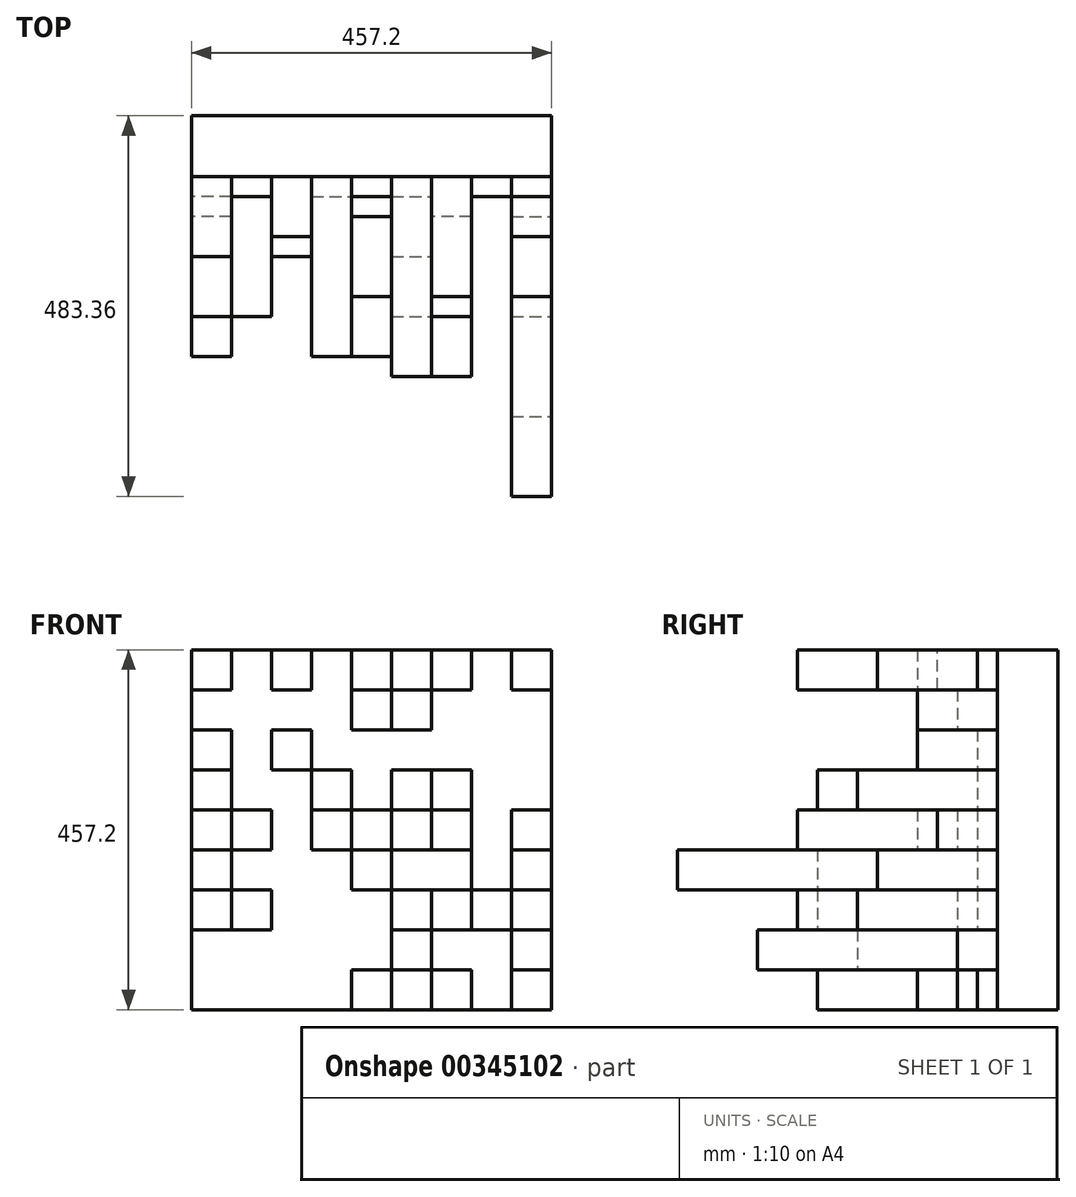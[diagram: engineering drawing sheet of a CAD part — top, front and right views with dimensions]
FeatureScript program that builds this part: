
annotation { "Feature Type Name" : "Feature", "Feature Type Description" : "" }
export const myFeature = defineFeature(function(context is Context, id is Id, definition is map)
    precondition{}
    {
        {
            var Q0;
            Q0=qCreatedBy(makeId("Front.planeOp"),FACE);
            var sketch = newSketch(context, id + "F0", { "sketchPlane" : qUnion([Q0])});
            skLineSegment(sketch, "E0.bottom", {"start": v(-369.5, 379.45) * mm, "end": v(87.7, 379.45) * mm});
            skLineSegment(sketch, "E0.top", {"start": v(-369.5, -77.75) * mm, "end": v(87.7, -77.75) * mm});
            skLineSegment(sketch, "E0.left", {"start": v(-369.5, 379.45) * mm, "end": v(-369.5, -77.75) * mm});
            skLineSegment(sketch, "E0.right", {"start": v(87.7, 379.45) * mm, "end": v(87.7, -77.75) * mm});
            skSolve(sketch);
        }
        {
            var Q0;
            Q0=makeQuery(id+"F0.imprint","IMPRINT",FACE,{"disambiguationData":[TD([[makeQuery(id+"F0.imprint","IMPRINT",EDGE,{"derivedFrom":sQuery(id+"F0.wireOp",EDGE,"E0.bottom")}),-1.0]])]});
            extrude(context, id + "F1", {"entities" : qUnion([Q0]), "depth" : 76.96 * mm});
        }
        {
            var Q0;
            Q0=makeQuery(id+"F1.opExtrude","CAP_FACE",FACE,{"disambiguationData":[OSD([sQuery(id+"F0.wireOp",EDGE,"E0.bottom"),sQuery(id+"F0.wireOp",EDGE,"E0.top"),sQuery(id+"F0.wireOp",EDGE,"E0.left"),sQuery(id+"F0.wireOp",EDGE,"E0.right")])],"isStart":false});
            var sketch = newSketch(context, id + "F2", { "sketchPlane" : qUnion([Q0])});
            skLineSegment(sketch, "E1.bottom", {"start": v(-369.5, 379.45) * mm, "end": v(-318.7, 379.45) * mm});
            skLineSegment(sketch, "E1.top", {"start": v(-369.5, 328.65) * mm, "end": v(-318.7, 328.65) * mm});
            skLineSegment(sketch, "E1.left", {"start": v(-369.5, 379.45) * mm, "end": v(-369.5, 328.65) * mm});
            skLineSegment(sketch, "E1.right", {"start": v(-318.7, 379.45) * mm, "end": v(-318.7, 328.65) * mm});
            skLineSegment(sketch, "E2.bottom", {"start": v(-318.7, 328.65) * mm, "end": v(-369.5, 328.65) * mm});
            skLineSegment(sketch, "E2.top", {"start": v(-318.7, 277.85) * mm, "end": v(-369.5, 277.85) * mm});
            skLineSegment(sketch, "E2.left", {"start": v(-318.7, 328.65) * mm, "end": v(-318.7, 277.85) * mm});
            skLineSegment(sketch, "E2.right", {"start": v(-369.5, 328.65) * mm, "end": v(-369.5, 277.85) * mm});
            skLineSegment(sketch, "E3.top", {"start": v(-318.7, 227.05) * mm, "end": v(-369.5, 227.05) * mm});
            skLineSegment(sketch, "E3.left", {"start": v(-318.7, 277.85) * mm, "end": v(-318.7, 227.05) * mm});
            skLineSegment(sketch, "E3.right", {"start": v(-369.5, 277.85) * mm, "end": v(-369.5, 227.05) * mm});
            skLineSegment(sketch, "E4.top", {"start": v(-318.7, 176.25) * mm, "end": v(-369.5, 176.25) * mm});
            skLineSegment(sketch, "E4.left", {"start": v(-318.7, 227.05) * mm, "end": v(-318.7, 176.25) * mm});
            skLineSegment(sketch, "E4.right", {"start": v(-369.5, 227.05) * mm, "end": v(-369.5, 176.25) * mm});
            skLineSegment(sketch, "E5.top", {"start": v(-318.7, 125.45) * mm, "end": v(-369.5, 125.45) * mm});
            skLineSegment(sketch, "E5.left", {"start": v(-318.7, 176.25) * mm, "end": v(-318.7, 125.45) * mm});
            skLineSegment(sketch, "E5.right", {"start": v(-369.5, 176.25) * mm, "end": v(-369.5, 125.45) * mm});
            skLineSegment(sketch, "E6.top", {"start": v(-318.7, 74.65) * mm, "end": v(-369.5, 74.65) * mm});
            skLineSegment(sketch, "E6.left", {"start": v(-318.7, 125.45) * mm, "end": v(-318.7, 74.65) * mm});
            skLineSegment(sketch, "E6.right", {"start": v(-369.5, 125.45) * mm, "end": v(-369.5, 74.65) * mm});
            skLineSegment(sketch, "E7.top", {"start": v(-318.7, 23.85) * mm, "end": v(-369.5, 23.85) * mm});
            skLineSegment(sketch, "E7.left", {"start": v(-318.7, 74.65) * mm, "end": v(-318.7, 23.85) * mm});
            skLineSegment(sketch, "E7.right", {"start": v(-369.5, 74.65) * mm, "end": v(-369.5, 23.85) * mm});
            skLineSegment(sketch, "E8.top", {"start": v(-318.7, -26.95) * mm, "end": v(-369.5, -26.95) * mm});
            skLineSegment(sketch, "E8.left", {"start": v(-318.7, 23.85) * mm, "end": v(-318.7, -26.95) * mm});
            skLineSegment(sketch, "E8.right", {"start": v(-369.5, 23.85) * mm, "end": v(-369.5, -26.95) * mm});
            skLineSegment(sketch, "E9.top", {"start": v(-318.7, -77.75) * mm, "end": v(-369.5, -77.75) * mm});
            skLineSegment(sketch, "E9.left", {"start": v(-318.7, -26.95) * mm, "end": v(-318.7, -77.75) * mm});
            skLineSegment(sketch, "E9.right", {"start": v(-369.5, -26.95) * mm, "end": v(-369.5, -77.75) * mm});
            skLineSegment(sketch, "E10.bottom", {"start": v(-318.7, -26.95) * mm, "end": v(-267.9, -26.95) * mm});
            skLineSegment(sketch, "E10.top", {"start": v(-318.7, 23.85) * mm, "end": v(-267.9, 23.85) * mm});
            skLineSegment(sketch, "E10.left", {"start": v(-318.7, -26.95) * mm, "end": v(-318.7, 23.85) * mm});
            skLineSegment(sketch, "E10.right", {"start": v(-267.9, -26.95) * mm, "end": v(-267.9, 23.85) * mm});
            skLineSegment(sketch, "E11.bottom", {"start": v(-267.9, -26.95) * mm, "end": v(-318.7, -26.95) * mm});
            skLineSegment(sketch, "E11.top", {"start": v(-267.9, -77.75) * mm, "end": v(-318.7, -77.75) * mm});
            skLineSegment(sketch, "E11.left", {"start": v(-267.9, -26.95) * mm, "end": v(-267.9, -77.75) * mm});
            skLineSegment(sketch, "E12.top", {"start": v(-318.7, 74.65) * mm, "end": v(-267.9, 74.65) * mm});
            skLineSegment(sketch, "E12.left", {"start": v(-318.7, 23.85) * mm, "end": v(-318.7, 74.65) * mm});
            skLineSegment(sketch, "E12.right", {"start": v(-267.9, 23.85) * mm, "end": v(-267.9, 74.65) * mm});
            skLineSegment(sketch, "E13.top", {"start": v(-318.7, 125.45) * mm, "end": v(-267.9, 125.45) * mm});
            skLineSegment(sketch, "E13.left", {"start": v(-318.7, 74.65) * mm, "end": v(-318.7, 125.45) * mm});
            skLineSegment(sketch, "E13.right", {"start": v(-267.9, 74.65) * mm, "end": v(-267.9, 125.45) * mm});
            skLineSegment(sketch, "E14.top", {"start": v(-318.7, 176.25) * mm, "end": v(-267.9, 176.25) * mm});
            skLineSegment(sketch, "E14.left", {"start": v(-318.7, 125.45) * mm, "end": v(-318.7, 176.25) * mm});
            skLineSegment(sketch, "E14.right", {"start": v(-267.9, 125.45) * mm, "end": v(-267.9, 176.25) * mm});
            skLineSegment(sketch, "E15.top", {"start": v(-318.7, 227.05) * mm, "end": v(-267.9, 227.05) * mm});
            skLineSegment(sketch, "E15.left", {"start": v(-318.7, 176.25) * mm, "end": v(-318.7, 227.05) * mm});
            skLineSegment(sketch, "E15.right", {"start": v(-267.9, 176.25) * mm, "end": v(-267.9, 227.05) * mm});
            skLineSegment(sketch, "E16.top", {"start": v(-318.7, 277.85) * mm, "end": v(-267.9, 277.85) * mm});
            skLineSegment(sketch, "E16.left", {"start": v(-318.7, 227.05) * mm, "end": v(-318.7, 277.85) * mm});
            skLineSegment(sketch, "E16.right", {"start": v(-267.9, 227.05) * mm, "end": v(-267.9, 277.85) * mm});
            skLineSegment(sketch, "E17.top", {"start": v(-318.7, 328.65) * mm, "end": v(-267.9, 328.65) * mm});
            skLineSegment(sketch, "E17.left", {"start": v(-318.7, 277.85) * mm, "end": v(-318.7, 328.65) * mm});
            skLineSegment(sketch, "E17.right", {"start": v(-267.9, 277.85) * mm, "end": v(-267.9, 328.65) * mm});
            skLineSegment(sketch, "E18.top", {"start": v(-318.7, 379.45) * mm, "end": v(-267.9, 379.45) * mm});
            skLineSegment(sketch, "E18.left", {"start": v(-318.7, 328.65) * mm, "end": v(-318.7, 379.45) * mm});
            skLineSegment(sketch, "E18.right", {"start": v(-267.9, 328.65) * mm, "end": v(-267.9, 379.45) * mm});
            skLineSegment(sketch, "E19.bottom", {"start": v(-267.9, 227.05) * mm, "end": v(-217.1, 227.05) * mm});
            skLineSegment(sketch, "E19.top", {"start": v(-267.9, 176.25) * mm, "end": v(-217.1, 176.25) * mm});
            skLineSegment(sketch, "E19.left", {"start": v(-267.9, 227.05) * mm, "end": v(-267.9, 176.25) * mm});
            skLineSegment(sketch, "E19.right", {"start": v(-217.1, 227.05) * mm, "end": v(-217.1, 176.25) * mm});
            skLineSegment(sketch, "E20.top", {"start": v(-267.9, 277.85) * mm, "end": v(-217.1, 277.85) * mm});
            skLineSegment(sketch, "E20.right", {"start": v(-217.1, 227.05) * mm, "end": v(-217.1, 277.85) * mm});
            skLineSegment(sketch, "E21.top", {"start": v(-267.9, 328.65) * mm, "end": v(-217.1, 328.65) * mm});
            skLineSegment(sketch, "E21.right", {"start": v(-217.1, 277.85) * mm, "end": v(-217.1, 328.65) * mm});
            skLineSegment(sketch, "E22.top", {"start": v(-267.9, 379.45) * mm, "end": v(-217.1, 379.45) * mm});
            skLineSegment(sketch, "E22.right", {"start": v(-217.1, 328.65) * mm, "end": v(-217.1, 379.45) * mm});
            skLineSegment(sketch, "E23.top", {"start": v(-267.9, 125.45) * mm, "end": v(-217.1, 125.45) * mm});
            skLineSegment(sketch, "E23.left", {"start": v(-267.9, 176.25) * mm, "end": v(-267.9, 125.45) * mm});
            skLineSegment(sketch, "E23.right", {"start": v(-217.1, 176.25) * mm, "end": v(-217.1, 125.45) * mm});
            skLineSegment(sketch, "E24.top", {"start": v(-267.9, 74.65) * mm, "end": v(-217.1, 74.65) * mm});
            skLineSegment(sketch, "E24.left", {"start": v(-267.9, 125.45) * mm, "end": v(-267.9, 74.65) * mm});
            skLineSegment(sketch, "E24.right", {"start": v(-217.1, 125.45) * mm, "end": v(-217.1, 74.65) * mm});
            skLineSegment(sketch, "E25.top", {"start": v(-267.9, 23.85) * mm, "end": v(-217.1, 23.85) * mm});
            skLineSegment(sketch, "E25.left", {"start": v(-267.9, 74.65) * mm, "end": v(-267.9, 23.85) * mm});
            skLineSegment(sketch, "E25.right", {"start": v(-217.1, 74.65) * mm, "end": v(-217.1, 23.85) * mm});
            skLineSegment(sketch, "E26.top", {"start": v(-267.9, -26.95) * mm, "end": v(-217.1, -26.95) * mm});
            skLineSegment(sketch, "E26.left", {"start": v(-267.9, 23.85) * mm, "end": v(-267.9, -26.95) * mm});
            skLineSegment(sketch, "E26.right", {"start": v(-217.1, 23.85) * mm, "end": v(-217.1, -26.95) * mm});
            skLineSegment(sketch, "E27.top", {"start": v(-267.9, -77.75) * mm, "end": v(-217.1, -77.75) * mm});
            skLineSegment(sketch, "E27.right", {"start": v(-217.1, -26.95) * mm, "end": v(-217.1, -77.75) * mm});
            skLineSegment(sketch, "E28.bottom", {"start": v(-217.1, 328.65) * mm, "end": v(-166.3, 328.65) * mm});
            skLineSegment(sketch, "E28.top", {"start": v(-217.1, 379.45) * mm, "end": v(-166.3, 379.45) * mm});
            skLineSegment(sketch, "E28.right", {"start": v(-166.3, 328.65) * mm, "end": v(-166.3, 379.45) * mm});
            skLineSegment(sketch, "E29.top", {"start": v(-217.1, 277.85) * mm, "end": v(-166.3, 277.85) * mm});
            skLineSegment(sketch, "E29.left", {"start": v(-217.1, 328.65) * mm, "end": v(-217.1, 277.85) * mm});
            skLineSegment(sketch, "E29.right", {"start": v(-166.3, 328.65) * mm, "end": v(-166.3, 277.85) * mm});
            skLineSegment(sketch, "E30.top", {"start": v(-217.1, 227.05) * mm, "end": v(-166.3, 227.05) * mm});
            skLineSegment(sketch, "E30.left", {"start": v(-217.1, 277.85) * mm, "end": v(-217.1, 227.05) * mm});
            skLineSegment(sketch, "E30.right", {"start": v(-166.3, 277.85) * mm, "end": v(-166.3, 227.05) * mm});
            skLineSegment(sketch, "E31.top", {"start": v(-217.1, 176.25) * mm, "end": v(-166.3, 176.25) * mm});
            skLineSegment(sketch, "E31.right", {"start": v(-166.3, 227.05) * mm, "end": v(-166.3, 176.25) * mm});
            skLineSegment(sketch, "E32.top", {"start": v(-217.1, 125.45) * mm, "end": v(-166.3, 125.45) * mm});
            skLineSegment(sketch, "E32.right", {"start": v(-166.3, 176.25) * mm, "end": v(-166.3, 125.45) * mm});
            skLineSegment(sketch, "E33.top", {"start": v(-217.1, 74.65) * mm, "end": v(-166.3, 74.65) * mm});
            skLineSegment(sketch, "E33.right", {"start": v(-166.3, 125.45) * mm, "end": v(-166.3, 74.65) * mm});
            skLineSegment(sketch, "E34.top", {"start": v(-217.1, 23.85) * mm, "end": v(-166.3, 23.85) * mm});
            skLineSegment(sketch, "E34.right", {"start": v(-166.3, 74.65) * mm, "end": v(-166.3, 23.85) * mm});
            skLineSegment(sketch, "E35.top", {"start": v(-217.1, -26.95) * mm, "end": v(-166.3, -26.95) * mm});
            skLineSegment(sketch, "E35.right", {"start": v(-166.3, 23.85) * mm, "end": v(-166.3, -26.95) * mm});
            skLineSegment(sketch, "E36.top", {"start": v(-217.1, -77.75) * mm, "end": v(-166.3, -77.75) * mm});
            skLineSegment(sketch, "E36.right", {"start": v(-166.3, -26.95) * mm, "end": v(-166.3, -77.75) * mm});
            skLineSegment(sketch, "E37.bottom", {"start": v(-166.3, 328.65) * mm, "end": v(-115.5, 328.65) * mm});
            skLineSegment(sketch, "E37.top", {"start": v(-166.3, 379.45) * mm, "end": v(-115.5, 379.45) * mm});
            skLineSegment(sketch, "E37.right", {"start": v(-115.5, 328.65) * mm, "end": v(-115.5, 379.45) * mm});
            skLineSegment(sketch, "E38.top", {"start": v(-166.3, 277.85) * mm, "end": v(-115.5, 277.85) * mm});
            skLineSegment(sketch, "E38.right", {"start": v(-115.5, 328.65) * mm, "end": v(-115.5, 277.85) * mm});
            skLineSegment(sketch, "E39.top", {"start": v(-166.3, 227.05) * mm, "end": v(-115.5, 227.05) * mm});
            skLineSegment(sketch, "E39.right", {"start": v(-115.5, 277.85) * mm, "end": v(-115.5, 227.05) * mm});
            skLineSegment(sketch, "E40.top", {"start": v(-166.3, 176.25) * mm, "end": v(-115.5, 176.25) * mm});
            skLineSegment(sketch, "E40.right", {"start": v(-115.5, 227.05) * mm, "end": v(-115.5, 176.25) * mm});
            skLineSegment(sketch, "E41.top", {"start": v(-166.3, 125.45) * mm, "end": v(-115.5, 125.45) * mm});
            skLineSegment(sketch, "E41.right", {"start": v(-115.5, 176.25) * mm, "end": v(-115.5, 125.45) * mm});
            skLineSegment(sketch, "E42.top", {"start": v(-166.3, 74.65) * mm, "end": v(-115.5, 74.65) * mm});
            skLineSegment(sketch, "E42.right", {"start": v(-115.5, 125.45) * mm, "end": v(-115.5, 74.65) * mm});
            skLineSegment(sketch, "E43.top", {"start": v(-166.3, 23.85) * mm, "end": v(-115.5, 23.85) * mm});
            skLineSegment(sketch, "E43.right", {"start": v(-115.5, 74.65) * mm, "end": v(-115.5, 23.85) * mm});
            skLineSegment(sketch, "E44.top", {"start": v(-166.3, -26.95) * mm, "end": v(-115.5, -26.95) * mm});
            skLineSegment(sketch, "E44.right", {"start": v(-115.5, 23.85) * mm, "end": v(-115.5, -26.95) * mm});
            skLineSegment(sketch, "E45.top", {"start": v(-166.3, -77.75) * mm, "end": v(-115.5, -77.75) * mm});
            skLineSegment(sketch, "E45.right", {"start": v(-115.5, -26.95) * mm, "end": v(-115.5, -77.75) * mm});
            skLineSegment(sketch, "E46.bottom", {"start": v(-115.5, -26.95) * mm, "end": v(-64.7, -26.95) * mm});
            skLineSegment(sketch, "E46.top", {"start": v(-115.5, -77.75) * mm, "end": v(-64.7, -77.75) * mm});
            skLineSegment(sketch, "E46.right", {"start": v(-64.7, -26.95) * mm, "end": v(-64.7, -77.75) * mm});
            skLineSegment(sketch, "E47.bottom", {"start": v(-115.5, 23.85) * mm, "end": v(-64.7, 23.85) * mm});
            skLineSegment(sketch, "E47.right", {"start": v(-64.7, 23.85) * mm, "end": v(-64.7, -26.95) * mm});
            skLineSegment(sketch, "E48.bottom", {"start": v(-115.5, 74.65) * mm, "end": v(-64.7, 74.65) * mm});
            skLineSegment(sketch, "E48.right", {"start": v(-64.7, 74.65) * mm, "end": v(-64.7, 23.85) * mm});
            skLineSegment(sketch, "E49.bottom", {"start": v(-115.5, 125.45) * mm, "end": v(-64.7, 125.45) * mm});
            skLineSegment(sketch, "E49.right", {"start": v(-64.7, 125.45) * mm, "end": v(-64.7, 74.65) * mm});
            skLineSegment(sketch, "E50.bottom", {"start": v(-115.5, 176.25) * mm, "end": v(-64.7, 176.25) * mm});
            skLineSegment(sketch, "E50.right", {"start": v(-64.7, 176.25) * mm, "end": v(-64.7, 125.45) * mm});
            skLineSegment(sketch, "E51.bottom", {"start": v(-115.5, 227.05) * mm, "end": v(-64.7, 227.05) * mm});
            skLineSegment(sketch, "E51.right", {"start": v(-64.7, 227.05) * mm, "end": v(-64.7, 176.25) * mm});
            skLineSegment(sketch, "E52.bottom", {"start": v(-115.5, 277.85) * mm, "end": v(-64.7, 277.85) * mm});
            skLineSegment(sketch, "E52.right", {"start": v(-64.7, 277.85) * mm, "end": v(-64.7, 227.05) * mm});
            skLineSegment(sketch, "E53.bottom", {"start": v(-115.5, 328.65) * mm, "end": v(-64.7, 328.65) * mm});
            skLineSegment(sketch, "E53.right", {"start": v(-64.7, 328.65) * mm, "end": v(-64.7, 277.85) * mm});
            skLineSegment(sketch, "E54.bottom", {"start": v(-115.5, 379.45) * mm, "end": v(-64.7, 379.45) * mm});
            skLineSegment(sketch, "E54.left", {"start": v(-115.5, 379.45) * mm, "end": v(-115.5, 328.65) * mm});
            skLineSegment(sketch, "E54.right", {"start": v(-64.7, 379.45) * mm, "end": v(-64.7, 328.65) * mm});
            skLineSegment(sketch, "E55.bottom", {"start": v(87.7, 379.45) * mm, "end": v(36.9, 379.45) * mm});
            skLineSegment(sketch, "E55.top", {"start": v(87.7, 328.65) * mm, "end": v(36.9, 328.65) * mm});
            skLineSegment(sketch, "E55.left", {"start": v(87.7, 379.45) * mm, "end": v(87.7, 328.65) * mm});
            skLineSegment(sketch, "E55.right", {"start": v(36.9, 379.45) * mm, "end": v(36.9, 328.65) * mm});
            skLineSegment(sketch, "E56.bottom", {"start": v(36.9, 328.65) * mm, "end": v(-13.9, 328.65) * mm});
            skLineSegment(sketch, "E56.top", {"start": v(36.9, 379.45) * mm, "end": v(-13.9, 379.45) * mm});
            skLineSegment(sketch, "E56.left", {"start": v(36.9, 328.65) * mm, "end": v(36.9, 379.45) * mm});
            skLineSegment(sketch, "E56.right", {"start": v(-13.9, 328.65) * mm, "end": v(-13.9, 379.45) * mm});
            skLineSegment(sketch, "E57.bottom", {"start": v(-13.9, 328.65) * mm, "end": v(-64.7, 328.65) * mm});
            skLineSegment(sketch, "E57.top", {"start": v(-13.9, 379.45) * mm, "end": v(-64.7, 379.45) * mm});
            skLineSegment(sketch, "E57.right", {"start": v(-64.7, 328.65) * mm, "end": v(-64.7, 379.45) * mm});
            skLineSegment(sketch, "E58.bottom", {"start": v(-64.7, 328.65) * mm, "end": v(-13.9, 328.65) * mm});
            skLineSegment(sketch, "E58.top", {"start": v(-64.7, 277.85) * mm, "end": v(-13.9, 277.85) * mm});
            skLineSegment(sketch, "E58.right", {"start": v(-13.9, 328.65) * mm, "end": v(-13.9, 277.85) * mm});
            skLineSegment(sketch, "E59.bottom", {"start": v(-13.9, 328.65) * mm, "end": v(36.9, 328.65) * mm});
            skLineSegment(sketch, "E59.top", {"start": v(-13.9, 277.85) * mm, "end": v(36.9, 277.85) * mm});
            skLineSegment(sketch, "E59.right", {"start": v(36.9, 328.65) * mm, "end": v(36.9, 277.85) * mm});
            skLineSegment(sketch, "E60.bottom", {"start": v(36.9, 328.65) * mm, "end": v(87.7, 328.65) * mm});
            skLineSegment(sketch, "E60.top", {"start": v(36.9, 277.85) * mm, "end": v(87.7, 277.85) * mm});
            skLineSegment(sketch, "E60.right", {"start": v(87.7, 328.65) * mm, "end": v(87.7, 277.85) * mm});
            skLineSegment(sketch, "E61.bottom", {"start": v(-13.9, 277.85) * mm, "end": v(-64.7, 277.85) * mm});
            skLineSegment(sketch, "E61.top", {"start": v(-13.9, 227.05) * mm, "end": v(-64.7, 227.05) * mm});
            skLineSegment(sketch, "E61.left", {"start": v(-13.9, 277.85) * mm, "end": v(-13.9, 227.05) * mm});
            skLineSegment(sketch, "E62.top", {"start": v(-13.9, 176.25) * mm, "end": v(-64.7, 176.25) * mm});
            skLineSegment(sketch, "E62.left", {"start": v(-13.9, 227.05) * mm, "end": v(-13.9, 176.25) * mm});
            skLineSegment(sketch, "E63.top", {"start": v(-13.9, 125.45) * mm, "end": v(-64.7, 125.45) * mm});
            skLineSegment(sketch, "E63.left", {"start": v(-13.9, 176.25) * mm, "end": v(-13.9, 125.45) * mm});
            skLineSegment(sketch, "E64.top", {"start": v(-13.9, 74.65) * mm, "end": v(-64.7, 74.65) * mm});
            skLineSegment(sketch, "E64.left", {"start": v(-13.9, 125.45) * mm, "end": v(-13.9, 74.65) * mm});
            skLineSegment(sketch, "E65.top", {"start": v(-13.9, 23.85) * mm, "end": v(-64.7, 23.85) * mm});
            skLineSegment(sketch, "E65.left", {"start": v(-13.9, 74.65) * mm, "end": v(-13.9, 23.85) * mm});
            skLineSegment(sketch, "E66.top", {"start": v(-13.9, -26.95) * mm, "end": v(-64.7, -26.95) * mm});
            skLineSegment(sketch, "E66.left", {"start": v(-13.9, 23.85) * mm, "end": v(-13.9, -26.95) * mm});
            skLineSegment(sketch, "E67.top", {"start": v(-13.9, 227.05) * mm, "end": v(36.9, 227.05) * mm});
            skLineSegment(sketch, "E67.right", {"start": v(36.9, 277.85) * mm, "end": v(36.9, 227.05) * mm});
            skLineSegment(sketch, "E68.top", {"start": v(36.9, 227.05) * mm, "end": v(87.7, 227.05) * mm});
            skLineSegment(sketch, "E68.right", {"start": v(87.7, 277.85) * mm, "end": v(87.7, 227.05) * mm});
            skLineSegment(sketch, "E69.bottom", {"start": v(36.9, 227.05) * mm, "end": v(-13.9, 227.05) * mm});
            skLineSegment(sketch, "E69.top", {"start": v(36.9, 176.25) * mm, "end": v(-13.9, 176.25) * mm});
            skLineSegment(sketch, "E69.left", {"start": v(36.9, 227.05) * mm, "end": v(36.9, 176.25) * mm});
            skLineSegment(sketch, "E70.bottom", {"start": v(-13.9, 176.25) * mm, "end": v(36.9, 176.25) * mm});
            skLineSegment(sketch, "E70.top", {"start": v(-13.9, 125.45) * mm, "end": v(36.9, 125.45) * mm});
            skLineSegment(sketch, "E70.right", {"start": v(36.9, 176.25) * mm, "end": v(36.9, 125.45) * mm});
            skLineSegment(sketch, "E71.bottom", {"start": v(-13.9, 74.65) * mm, "end": v(36.9, 74.65) * mm});
            skLineSegment(sketch, "E71.left", {"start": v(-13.9, 74.65) * mm, "end": v(-13.9, 125.45) * mm});
            skLineSegment(sketch, "E71.right", {"start": v(36.9, 74.65) * mm, "end": v(36.9, 125.45) * mm});
            skLineSegment(sketch, "E72.bottom", {"start": v(-13.9, 23.85) * mm, "end": v(36.9, 23.85) * mm});
            skLineSegment(sketch, "E72.left", {"start": v(-13.9, 23.85) * mm, "end": v(-13.9, 74.65) * mm});
            skLineSegment(sketch, "E72.right", {"start": v(36.9, 23.85) * mm, "end": v(36.9, 74.65) * mm});
            skLineSegment(sketch, "E73.top", {"start": v(-13.9, -77.75) * mm, "end": v(-64.7, -77.75) * mm});
            skLineSegment(sketch, "E73.left", {"start": v(-13.9, -26.95) * mm, "end": v(-13.9, -77.75) * mm});
            skLineSegment(sketch, "E74.bottom", {"start": v(-13.9, -26.95) * mm, "end": v(36.9, -26.95) * mm});
            skLineSegment(sketch, "E74.left", {"start": v(-13.9, -26.95) * mm, "end": v(-13.9, 23.85) * mm});
            skLineSegment(sketch, "E74.right", {"start": v(36.9, -26.95) * mm, "end": v(36.9, 23.85) * mm});
            skLineSegment(sketch, "E75.top", {"start": v(-13.9, -77.75) * mm, "end": v(36.9, -77.75) * mm});
            skLineSegment(sketch, "E75.right", {"start": v(36.9, -26.95) * mm, "end": v(36.9, -77.75) * mm});
            skLineSegment(sketch, "E76.bottom", {"start": v(36.9, -26.95) * mm, "end": v(87.7, -26.95) * mm});
            skLineSegment(sketch, "E76.top", {"start": v(36.9, -77.75) * mm, "end": v(87.7, -77.75) * mm});
            skLineSegment(sketch, "E76.right", {"start": v(87.7, -26.95) * mm, "end": v(87.7, -77.75) * mm});
            skLineSegment(sketch, "E77.top", {"start": v(36.9, 23.85) * mm, "end": v(87.7, 23.85) * mm});
            skLineSegment(sketch, "E77.right", {"start": v(87.7, -26.95) * mm, "end": v(87.7, 23.85) * mm});
            skLineSegment(sketch, "E78.top", {"start": v(36.9, 74.65) * mm, "end": v(87.7, 74.65) * mm});
            skLineSegment(sketch, "E78.right", {"start": v(87.7, 23.85) * mm, "end": v(87.7, 74.65) * mm});
            skLineSegment(sketch, "E79.top", {"start": v(36.9, 125.45) * mm, "end": v(87.7, 125.45) * mm});
            skLineSegment(sketch, "E79.right", {"start": v(87.7, 74.65) * mm, "end": v(87.7, 125.45) * mm});
            skLineSegment(sketch, "E80.top", {"start": v(36.9, 176.25) * mm, "end": v(87.7, 176.25) * mm});
            skLineSegment(sketch, "E80.left", {"start": v(36.9, 125.45) * mm, "end": v(36.9, 176.25) * mm});
            skLineSegment(sketch, "E80.right", {"start": v(87.7, 125.45) * mm, "end": v(87.7, 176.25) * mm});
            skLineSegment(sketch, "E81.left", {"start": v(36.9, 176.25) * mm, "end": v(36.9, 227.05) * mm});
            skLineSegment(sketch, "E81.right", {"start": v(87.7, 176.25) * mm, "end": v(87.7, 227.05) * mm});
            skSolve(sketch);
        }
        {
            var Q0;
            Q0=makeQuery(id+"F2.imprint","IMPRINT",FACE,{"disambiguationData":[TD([[makeQuery(id+"F2.imprint","IMPRINT",EDGE,{"derivedFrom":sQuery(id+"F2.wireOp",EDGE,"E1.bottom")}),-1.0]])]});
            var Q1;
            Q1=makeQuery(id+"F2.imprint","IMPRINT",FACE,{"disambiguationData":[TD([[makeQuery(id+"F2.imprint","IMPRINT",EDGE,{"derivedFrom":sQuery(id+"F2.wireOp",EDGE,"E19.bottom")}),1.0]])]});
            var Q2;
            Q2=makeQuery(id+"F2.imprint","IMPRINT",FACE,{"disambiguationData":[TD([[makeQuery(id+"F2.imprint","IMPRINT",EDGE,{"derivedFrom":sQuery(id+"F2.wireOp",EDGE,"E49.bottom")}),1.0]])]});
            var Q3;
            Q3=makeQuery(id+"F2.imprint","IMPRINT",FACE,{"disambiguationData":[TD([[makeQuery(id+"F2.imprint","IMPRINT",EDGE,{"derivedFrom":sQuery(id+"F2.wireOp",EDGE,"E33.top")}),-1.0]])]});
            var Q4;
            Q4=makeQuery(id+"F2.imprint","IMPRINT",FACE,{"disambiguationData":[TD([[makeQuery(id+"F2.imprint","IMPRINT",EDGE,{"derivedFrom":sQuery(id+"F2.wireOp",EDGE,"E7.top")}),1.0]])]});
            var Q5;
            Q5=makeQuery(id+"F2.imprint","IMPRINT",FACE,{"disambiguationData":[TD([[makeQuery(id+"F2.imprint","IMPRINT",EDGE,{"derivedFrom":sQuery(id+"F2.wireOp",EDGE,"E46.top")}),1.0]])]});
            var Q6;
            Q6=makeQuery(id+"F2.imprint","IMPRINT",FACE,{"disambiguationData":[TD([[makeQuery(id+"F2.imprint","IMPRINT",EDGE,{"derivedFrom":sQuery(id+"F2.wireOp",EDGE,"E80.top")}),1.0]])]});
            var Q7;
            Q7=makeQuery(id+"F2.imprint","IMPRINT",FACE,{"disambiguationData":[TD([[makeQuery(id+"F2.imprint","IMPRINT",EDGE,{"derivedFrom":sQuery(id+"F2.wireOp",EDGE,"E52.bottom")}),1.0]])]});
            extrude(context, id + "F3", {"entities" : qUnion([Q0, Q1, Q2, Q3, Q4, Q5, Q6, Q7]), "depth" : 101.6 * mm});
        }
        {
            var Q0;
            Q0=makeQuery(id+"F2.imprint","IMPRINT",FACE,{"disambiguationData":[TD([[makeQuery(id+"F2.imprint","IMPRINT",EDGE,{"derivedFrom":sQuery(id+"F2.wireOp",EDGE,"E2.top")}),1.0]])]});
            var Q1;
            Q1=makeQuery(id+"F2.imprint","IMPRINT",FACE,{"disambiguationData":[TD([[makeQuery(id+"F2.imprint","IMPRINT",EDGE,{"derivedFrom":sQuery(id+"F2.wireOp",EDGE,"E31.top")}),-1.0]])]});
            var Q2;
            Q2=makeQuery(id+"F2.imprint","IMPRINT",FACE,{"disambiguationData":[TD([[makeQuery(id+"F2.imprint","IMPRINT",EDGE,{"derivedFrom":sQuery(id+"F2.wireOp",EDGE,"E50.bottom")}),1.0]])]});
            var Q3;
            Q3=makeQuery(id+"F2.imprint","IMPRINT",FACE,{"disambiguationData":[TD([[makeQuery(id+"F2.imprint","IMPRINT",EDGE,{"derivedFrom":sQuery(id+"F2.wireOp",EDGE,"E55.bottom")}),-1.0]])]});
            var Q4;
            Q4=makeQuery(id+"F2.imprint","IMPRINT",FACE,{"disambiguationData":[TD([[makeQuery(id+"F2.imprint","IMPRINT",EDGE,{"derivedFrom":sQuery(id+"F2.wireOp",EDGE,"E37.top")}),-1.0]])]});
            var Q5;
            Q5=makeQuery(id+"F2.imprint","IMPRINT",FACE,{"disambiguationData":[TD([[makeQuery(id+"F2.imprint","IMPRINT",EDGE,{"derivedFrom":sQuery(id+"F2.wireOp",EDGE,"E35.top")}),-1.0]])]});
            var Q6;
            Q6=makeQuery(id+"F2.imprint","IMPRINT",FACE,{"disambiguationData":[TD([[makeQuery(id+"F2.imprint","IMPRINT",EDGE,{"derivedFrom":sQuery(id+"F2.wireOp",EDGE,"E71.bottom")}),-1.0]])]});
            var Q7;
            Q7=makeQuery(id+"F2.imprint","IMPRINT",FACE,{"disambiguationData":[TD([[makeQuery(id+"F2.imprint","IMPRINT",EDGE,{"derivedFrom":sQuery(id+"F2.wireOp",EDGE,"E76.top")}),1.0]])]});
            var Q8;
            Q8=makeQuery(id+"F2.imprint","IMPRINT",FACE,{"disambiguationData":[TD([[makeQuery(id+"F2.imprint","IMPRINT",EDGE,{"derivedFrom":sQuery(id+"F2.wireOp",EDGE,"E13.top")}),1.0]])]});
            var Q9;
            Q9=makeQuery(id+"F2.imprint","IMPRINT",FACE,{"disambiguationData":[TD([[makeQuery(id+"F2.imprint","IMPRINT",EDGE,{"derivedFrom":sQuery(id+"F2.wireOp",EDGE,"E5.top")}),1.0]])]});
            extrude(context, id + "F4", {"entities" : qUnion([Q0, Q1, Q2, Q3, Q4, Q5, Q6, Q7, Q8, Q9]), "depth" : 25.4 * mm});
        }
        {
            var Q0;
            Q0=makeQuery(id+"F2.imprint","IMPRINT",FACE,{"disambiguationData":[TD([[makeQuery(id+"F2.imprint","IMPRINT",EDGE,{"derivedFrom":sQuery(id+"F2.wireOp",EDGE,"E28.bottom")}),-1.0]])]});
            var Q1;
            Q1=makeQuery(id+"F2.imprint","IMPRINT",FACE,{"disambiguationData":[TD([[makeQuery(id+"F2.imprint","IMPRINT",EDGE,{"derivedFrom":sQuery(id+"F2.wireOp",EDGE,"E60.top")}),-1.0]])]});
            var Q2;
            Q2=makeQuery(id+"F2.imprint","IMPRINT",FACE,{"disambiguationData":[TD([[makeQuery(id+"F2.imprint","IMPRINT",EDGE,{"derivedFrom":sQuery(id+"F2.wireOp",EDGE,"E57.top")}),-1.0]])]});
            var Q3;
            Q3=makeQuery(id+"F2.imprint","IMPRINT",FACE,{"disambiguationData":[TD([[makeQuery(id+"F2.imprint","IMPRINT",EDGE,{"derivedFrom":sQuery(id+"F2.wireOp",EDGE,"E11.bottom")}),1.0]])]});
            var Q4;
            Q4=makeQuery(id+"F2.imprint","IMPRINT",FACE,{"disambiguationData":[TD([[makeQuery(id+"F2.imprint","IMPRINT",EDGE,{"derivedFrom":sQuery(id+"F2.wireOp",EDGE,"E41.top")}),-1.0]])]});
            var Q5;
            Q5=makeQuery(id+"F2.imprint","IMPRINT",FACE,{"disambiguationData":[TD([[makeQuery(id+"F2.imprint","IMPRINT",EDGE,{"derivedFrom":sQuery(id+"F2.wireOp",EDGE,"E78.top")}),1.0]])]});
            extrude(context, id + "F5", {"entities" : qUnion([Q0, Q1, Q2, Q3, Q4, Q5]), "depth" : 152.4 * mm});
        }
        {
            var Q0;
            Q0=makeQuery(id+"F2.imprint","IMPRINT",FACE,{"disambiguationData":[TD([[makeQuery(id+"F2.imprint","IMPRINT",EDGE,{"derivedFrom":sQuery(id+"F2.wireOp",EDGE,"E8.top")}),1.0]])]});
            var Q1;
            Q1=makeQuery(id+"F2.imprint","IMPRINT",FACE,{"disambiguationData":[TD([[makeQuery(id+"F2.imprint","IMPRINT",EDGE,{"derivedFrom":sQuery(id+"F2.wireOp",EDGE,"E43.top")}),-1.0]])]});
            var Q2;
            Q2=makeQuery(id+"F2.imprint","IMPRINT",FACE,{"disambiguationData":[TD([[makeQuery(id+"F2.imprint","IMPRINT",EDGE,{"derivedFrom":sQuery(id+"F2.wireOp",EDGE,"E12.top")}),1.0]])]});
            var Q3;
            Q3=makeQuery(id+"F2.imprint","IMPRINT",FACE,{"disambiguationData":[TD([[makeQuery(id+"F2.imprint","IMPRINT",EDGE,{"derivedFrom":sQuery(id+"F2.wireOp",EDGE,"E20.top")}),1.0]])]});
            var Q4;
            Q4=makeQuery(id+"F2.imprint","IMPRINT",FACE,{"disambiguationData":[TD([[makeQuery(id+"F2.imprint","IMPRINT",EDGE,{"derivedFrom":sQuery(id+"F2.wireOp",EDGE,"E14.top")}),1.0]])]});
            var Q5;
            Q5=makeQuery(id+"F2.imprint","IMPRINT",FACE,{"disambiguationData":[TD([[makeQuery(id+"F2.imprint","IMPRINT",EDGE,{"derivedFrom":sQuery(id+"F2.wireOp",EDGE,"E79.top")}),1.0]])]});
            var Q6;
            Q6=makeQuery(id+"F2.imprint","IMPRINT",FACE,{"disambiguationData":[TD([[makeQuery(id+"F2.imprint","IMPRINT",EDGE,{"derivedFrom":sQuery(id+"F2.wireOp",EDGE,"E74.bottom")}),-1.0]])]});
            var Q7;
            Q7=makeQuery(id+"F2.imprint","IMPRINT",FACE,{"disambiguationData":[TD([[makeQuery(id+"F2.imprint","IMPRINT",EDGE,{"derivedFrom":sQuery(id+"F2.wireOp",EDGE,"E69.bottom")}),1.0]])]});
            var Q8;
            Q8=makeQuery(id+"F2.imprint","IMPRINT",FACE,{"disambiguationData":[TD([[makeQuery(id+"F2.imprint","IMPRINT",EDGE,{"derivedFrom":sQuery(id+"F2.wireOp",EDGE,"E61.bottom")}),1.0]])]});
            var Q9;
            Q9=makeQuery(id+"F2.imprint","IMPRINT",FACE,{"disambiguationData":[TD([[makeQuery(id+"F2.imprint","IMPRINT",EDGE,{"derivedFrom":sQuery(id+"F2.wireOp",EDGE,"E21.top")}),1.0]])]});
            var Q10;
            Q10=makeQuery(id+"F2.imprint","IMPRINT",FACE,{"disambiguationData":[TD([[makeQuery(id+"F2.imprint","IMPRINT",EDGE,{"derivedFrom":sQuery(id+"F2.wireOp",EDGE,"E2.bottom")}),1.0]])]});
            extrude(context, id + "F6", {"entities" : qUnion([Q0, Q1, Q2, Q3, Q4, Q5, Q6, Q7, Q8, Q9, Q10]), "depth" : 76.2 * mm});
        }
        {
            var Q0;
            Q0=makeQuery(id+"F2.imprint","IMPRINT",FACE,{"disambiguationData":[TD([[makeQuery(id+"F2.imprint","IMPRINT",EDGE,{"derivedFrom":sQuery(id+"F2.wireOp",EDGE,"E25.top")}),-1.0]])]});
            var Q1;
            Q1=makeQuery(id+"F2.imprint","IMPRINT",FACE,{"disambiguationData":[TD([[makeQuery(id+"F2.imprint","IMPRINT",EDGE,{"derivedFrom":sQuery(id+"F2.wireOp",EDGE,"E61.top")}),1.0]])]});
            var Q2;
            Q2=makeQuery(id+"F2.imprint","IMPRINT",FACE,{"disambiguationData":[TD([[makeQuery(id+"F2.imprint","IMPRINT",EDGE,{"derivedFrom":sQuery(id+"F2.wireOp",EDGE,"E70.bottom")}),-1.0]])]});
            var Q3;
            Q3=makeQuery(id+"F2.imprint","IMPRINT",FACE,{"disambiguationData":[TD([[makeQuery(id+"F2.imprint","IMPRINT",EDGE,{"derivedFrom":sQuery(id+"F2.wireOp",EDGE,"E29.top")}),-1.0]])]});
            var Q4;
            Q4=makeQuery(id+"F2.imprint","IMPRINT",FACE,{"disambiguationData":[TD([[makeQuery(id+"F2.imprint","IMPRINT",EDGE,{"derivedFrom":sQuery(id+"F2.wireOp",EDGE,"E46.bottom")}),1.0]])]});
            var Q5;
            Q5=makeQuery(id+"F2.imprint","IMPRINT",FACE,{"disambiguationData":[TD([[makeQuery(id+"F2.imprint","IMPRINT",EDGE,{"derivedFrom":sQuery(id+"F2.wireOp",EDGE,"E77.top")}),1.0]])]});
            var Q6;
            Q6=makeQuery(id+"F2.imprint","IMPRINT",FACE,{"disambiguationData":[TD([[makeQuery(id+"F2.imprint","IMPRINT",EDGE,{"derivedFrom":sQuery(id+"F2.wireOp",EDGE,"E59.bottom")}),-1.0]])]});
            var Q7;
            Q7=makeQuery(id+"F2.imprint","IMPRINT",FACE,{"disambiguationData":[TD([[makeQuery(id+"F2.imprint","IMPRINT",EDGE,{"derivedFrom":sQuery(id+"F2.wireOp",EDGE,"E3.top")}),1.0]])]});
            var Q8;
            Q8=makeQuery(id+"F2.imprint","IMPRINT",FACE,{"disambiguationData":[TD([[makeQuery(id+"F2.imprint","IMPRINT",EDGE,{"derivedFrom":sQuery(id+"F2.wireOp",EDGE,"E10.top")}),1.0]])]});
            var Q9;
            Q9=makeQuery(id+"F2.imprint","IMPRINT",FACE,{"disambiguationData":[TD([[makeQuery(id+"F2.imprint","IMPRINT",EDGE,{"derivedFrom":sQuery(id+"F2.wireOp",EDGE,"E39.top")}),-1.0]])]});
            extrude(context, id + "F7", {"entities" : qUnion([Q0, Q1, Q2, Q3, Q4, Q5, Q6, Q7, Q8, Q9]), "depth" : 177.8 * mm});
        }
        {
            var Q0;
            Q0=makeQuery(id+"F2.imprint","IMPRINT",FACE,{"disambiguationData":[TD([[makeQuery(id+"F2.imprint","IMPRINT",EDGE,{"derivedFrom":sQuery(id+"F2.wireOp",EDGE,"E16.top")}),1.0]])]});
            var Q1;
            Q1=makeQuery(id+"F2.imprint","IMPRINT",FACE,{"disambiguationData":[TD([[makeQuery(id+"F2.imprint","IMPRINT",EDGE,{"derivedFrom":sQuery(id+"F2.wireOp",EDGE,"E32.top")}),-1.0]])]});
            var Q2;
            Q2=makeQuery(id+"F2.imprint","IMPRINT",FACE,{"disambiguationData":[TD([[makeQuery(id+"F2.imprint","IMPRINT",EDGE,{"derivedFrom":sQuery(id+"F2.wireOp",EDGE,"E40.top")}),-1.0]])]});
            var Q3;
            Q3=makeQuery(id+"F2.imprint","IMPRINT",FACE,{"disambiguationData":[TD([[makeQuery(id+"F2.imprint","IMPRINT",EDGE,{"derivedFrom":sQuery(id+"F2.wireOp",EDGE,"E37.bottom")}),-1.0]])]});
            var Q4;
            Q4=makeQuery(id+"F2.imprint","IMPRINT",FACE,{"disambiguationData":[TD([[makeQuery(id+"F2.imprint","IMPRINT",EDGE,{"derivedFrom":sQuery(id+"F2.wireOp",EDGE,"E66.top")}),1.0]])]});
            var Q5;
            Q5=makeQuery(id+"F2.imprint","IMPRINT",FACE,{"disambiguationData":[TD([[makeQuery(id+"F2.imprint","IMPRINT",EDGE,{"derivedFrom":sQuery(id+"F2.wireOp",EDGE,"E64.top")}),1.0]])]});
            var Q6;
            Q6=makeQuery(id+"F2.imprint","IMPRINT",FACE,{"disambiguationData":[TD([[makeQuery(id+"F2.imprint","IMPRINT",EDGE,{"derivedFrom":sQuery(id+"F2.wireOp",EDGE,"E76.bottom")}),1.0]])]});
            var Q7;
            Q7=makeQuery(id+"F2.imprint","IMPRINT",FACE,{"disambiguationData":[TD([[makeQuery(id+"F2.imprint","IMPRINT",EDGE,{"derivedFrom":sQuery(id+"F2.wireOp",EDGE,"E59.top")}),-1.0]])]});
            var Q8;
            Q8=makeQuery(id+"F2.imprint","IMPRINT",FACE,{"disambiguationData":[TD([[makeQuery(id+"F2.imprint","IMPRINT",EDGE,{"derivedFrom":sQuery(id+"F2.wireOp",EDGE,"E19.left")}),1.0]])]});
            var Q9;
            Q9=makeQuery(id+"F2.imprint","IMPRINT",FACE,{"disambiguationData":[TD([[makeQuery(id+"F2.imprint","IMPRINT",EDGE,{"derivedFrom":sQuery(id+"F2.wireOp",EDGE,"E24.top")}),-1.0]])]});
            var Q10;
            Q10=makeQuery(id+"F2.imprint","IMPRINT",FACE,{"disambiguationData":[TD([[makeQuery(id+"F2.imprint","IMPRINT",EDGE,{"derivedFrom":sQuery(id+"F2.wireOp",EDGE,"E4.top")}),1.0]])]});
            var Q11;
            Q11=makeQuery(id+"F2.imprint","IMPRINT",FACE,{"disambiguationData":[TD([[makeQuery(id+"F2.imprint","IMPRINT",EDGE,{"derivedFrom":sQuery(id+"F2.wireOp",EDGE,"E26.top")}),-1.0]])]});
            extrude(context, id + "F8", {"entities" : qUnion([Q0, Q1, Q2, Q3, Q4, Q5, Q6, Q7, Q8, Q9, Q10, Q11]), "depth" : 50.8 * mm});
        }
        {
            var Q0;
            Q0=makeQuery(id+"F2.imprint","IMPRINT",FACE,{"disambiguationData":[TD([[makeQuery(id+"F2.imprint","IMPRINT",EDGE,{"derivedFrom":sQuery(id+"F2.wireOp",EDGE,"E17.top")}),1.0]])]});
            var Q1;
            Q1=makeQuery(id+"F2.imprint","IMPRINT",FACE,{"disambiguationData":[TD([[makeQuery(id+"F2.imprint","IMPRINT",EDGE,{"derivedFrom":sQuery(id+"F2.wireOp",EDGE,"E42.top")}),-1.0]])]});
            var Q2;
            Q2=makeQuery(id+"F2.imprint","IMPRINT",FACE,{"disambiguationData":[TD([[makeQuery(id+"F2.imprint","IMPRINT",EDGE,{"derivedFrom":sQuery(id+"F2.wireOp",EDGE,"E44.top")}),-1.0]])]});
            var Q3;
            Q3=makeQuery(id+"F2.imprint","IMPRINT",FACE,{"disambiguationData":[TD([[makeQuery(id+"F2.imprint","IMPRINT",EDGE,{"derivedFrom":sQuery(id+"F2.wireOp",EDGE,"E63.top")}),1.0]])]});
            var Q4;
            Q4=makeQuery(id+"F2.imprint","IMPRINT",FACE,{"disambiguationData":[TD([[makeQuery(id+"F2.imprint","IMPRINT",EDGE,{"derivedFrom":sQuery(id+"F2.wireOp",EDGE,"E51.bottom")}),1.0]])]});
            var Q5;
            Q5=makeQuery(id+"F3.opExtrude","CAP_FACE",FACE,{"disambiguationData":[OSD([sQuery(id+"F2.wireOp",EDGE,"E80.top"),sQuery(id+"F2.wireOp",EDGE,"E68.top"),sQuery(id+"F2.wireOp",EDGE,"E81.left"),sQuery(id+"F2.wireOp",EDGE,"E81.right")])],"isStart":false});
            var Q6;
            Q6=makeQuery(id+"F2.imprint","IMPRINT",FACE,{"disambiguationData":[TD([[makeQuery(id+"F2.imprint","IMPRINT",EDGE,{"derivedFrom":sQuery(id+"F2.wireOp",EDGE,"E23.top")}),-1.0]])]});
            var Q7;
            Q7=makeQuery(id+"F2.imprint","IMPRINT",FACE,{"disambiguationData":[TD([[makeQuery(id+"F2.imprint","IMPRINT",EDGE,{"derivedFrom":sQuery(id+"F2.wireOp",EDGE,"E6.top")}),1.0]])]});
            var Q8;
            Q8=makeQuery(id+"F2.imprint","IMPRINT",FACE,{"disambiguationData":[TD([[makeQuery(id+"F2.imprint","IMPRINT",EDGE,{"derivedFrom":sQuery(id+"F2.wireOp",EDGE,"E15.top")}),1.0]])]});
            var Q9;
            Q9=makeQuery(id+"F2.imprint","IMPRINT",FACE,{"disambiguationData":[TD([[makeQuery(id+"F2.imprint","IMPRINT",EDGE,{"derivedFrom":sQuery(id+"F2.wireOp",EDGE,"E30.top")}),-1.0]])]});
            var Q10;
            Q10=makeQuery(id+"F2.imprint","IMPRINT",FACE,{"disambiguationData":[TD([[makeQuery(id+"F2.imprint","IMPRINT",EDGE,{"derivedFrom":sQuery(id+"F2.wireOp",EDGE,"E48.bottom")}),1.0]])]});
            extrude(context, id + "F9", {"entities" : qUnion([Q0, Q1, Q2, Q3, Q4, Q5, Q6, Q7, Q8, Q9, Q10]), "depth" : 228.6 * mm});
        }
        {
            var Q0;
            Q0=makeQuery(id+"F8.opExtrude","CAP_FACE",FACE,{"disambiguationData":[OSD([sQuery(id+"F2.wireOp",EDGE,"E24.top"),sQuery(id+"F2.wireOp",EDGE,"E25.left"),sQuery(id+"F2.wireOp",EDGE,"E25.top"),sQuery(id+"F2.wireOp",EDGE,"E25.right")])],"isStart":false});
            var Q1;
            Q1=makeQuery(id+"F2.imprint","IMPRINT",FACE,{"disambiguationData":[TD([[makeQuery(id+"F2.imprint","IMPRINT",EDGE,{"derivedFrom":sQuery(id+"F2.wireOp",EDGE,"E10.left")}),-1.0]])]});
            var Q2;
            Q2=makeQuery(id+"F2.imprint","IMPRINT",FACE,{"disambiguationData":[TD([[makeQuery(id+"F2.imprint","IMPRINT",EDGE,{"derivedFrom":sQuery(id+"F2.wireOp",EDGE,"E34.top")}),-1.0]])]});
            var Q3;
            Q3=makeQuery(id+"F2.imprint","IMPRINT",FACE,{"disambiguationData":[TD([[makeQuery(id+"F2.imprint","IMPRINT",EDGE,{"derivedFrom":sQuery(id+"F2.wireOp",EDGE,"E47.bottom")}),1.0]])]});
            var Q4;
            Q4=makeQuery(id+"F5.opExtrude","CAP_FACE",FACE,{"disambiguationData":[OSD([sQuery(id+"F2.wireOp",EDGE,"E78.top"),sQuery(id+"F2.wireOp",EDGE,"E71.right"),sQuery(id+"F2.wireOp",EDGE,"E79.right"),sQuery(id+"F2.wireOp",EDGE,"E79.top")])],"isStart":false});
            var Q5;
            Q5=makeQuery(id+"F2.imprint","IMPRINT",FACE,{"disambiguationData":[TD([[makeQuery(id+"F2.imprint","IMPRINT",EDGE,{"derivedFrom":sQuery(id+"F2.wireOp",EDGE,"E62.top")}),1.0]])]});
            var Q6;
            Q6=makeQuery(id+"F2.imprint","IMPRINT",FACE,{"disambiguationData":[TD([[makeQuery(id+"F2.imprint","IMPRINT",EDGE,{"derivedFrom":sQuery(id+"F2.wireOp",EDGE,"E58.bottom")}),-1.0]])]});
            var Q7;
            Q7=makeQuery(id+"F2.imprint","IMPRINT",FACE,{"disambiguationData":[TD([[makeQuery(id+"F2.imprint","IMPRINT",EDGE,{"derivedFrom":sQuery(id+"F2.wireOp",EDGE,"E38.top")}),-1.0]])]});
            var Q8;
            Q8=makeQuery(id+"F2.imprint","IMPRINT",FACE,{"disambiguationData":[TD([[makeQuery(id+"F2.imprint","IMPRINT",EDGE,{"derivedFrom":sQuery(id+"F2.wireOp",EDGE,"E54.bottom")}),-1.0]])]});
            var Q9;
            Q9=makeQuery(id+"F2.imprint","IMPRINT",FACE,{"disambiguationData":[TD([[makeQuery(id+"F2.imprint","IMPRINT",EDGE,{"derivedFrom":sQuery(id+"F2.wireOp",EDGE,"E70.top")}),-1.0]])]});
            var Q10;
            Q10=makeQuery(id+"F8.opExtrude","CAP_FACE",FACE,{"disambiguationData":[OSD([sQuery(id+"F2.wireOp",EDGE,"E76.bottom"),sQuery(id+"F2.wireOp",EDGE,"E74.right"),sQuery(id+"F2.wireOp",EDGE,"E77.right"),sQuery(id+"F2.wireOp",EDGE,"E77.top")])],"isStart":false});
            extrude(context, id + "F10", {"entities" : qUnion([Q0, Q1, Q2, Q3, Q4, Q5, Q6, Q7, Q8, Q9, Q10]), "depth" : 254 * mm});
        }
    });
